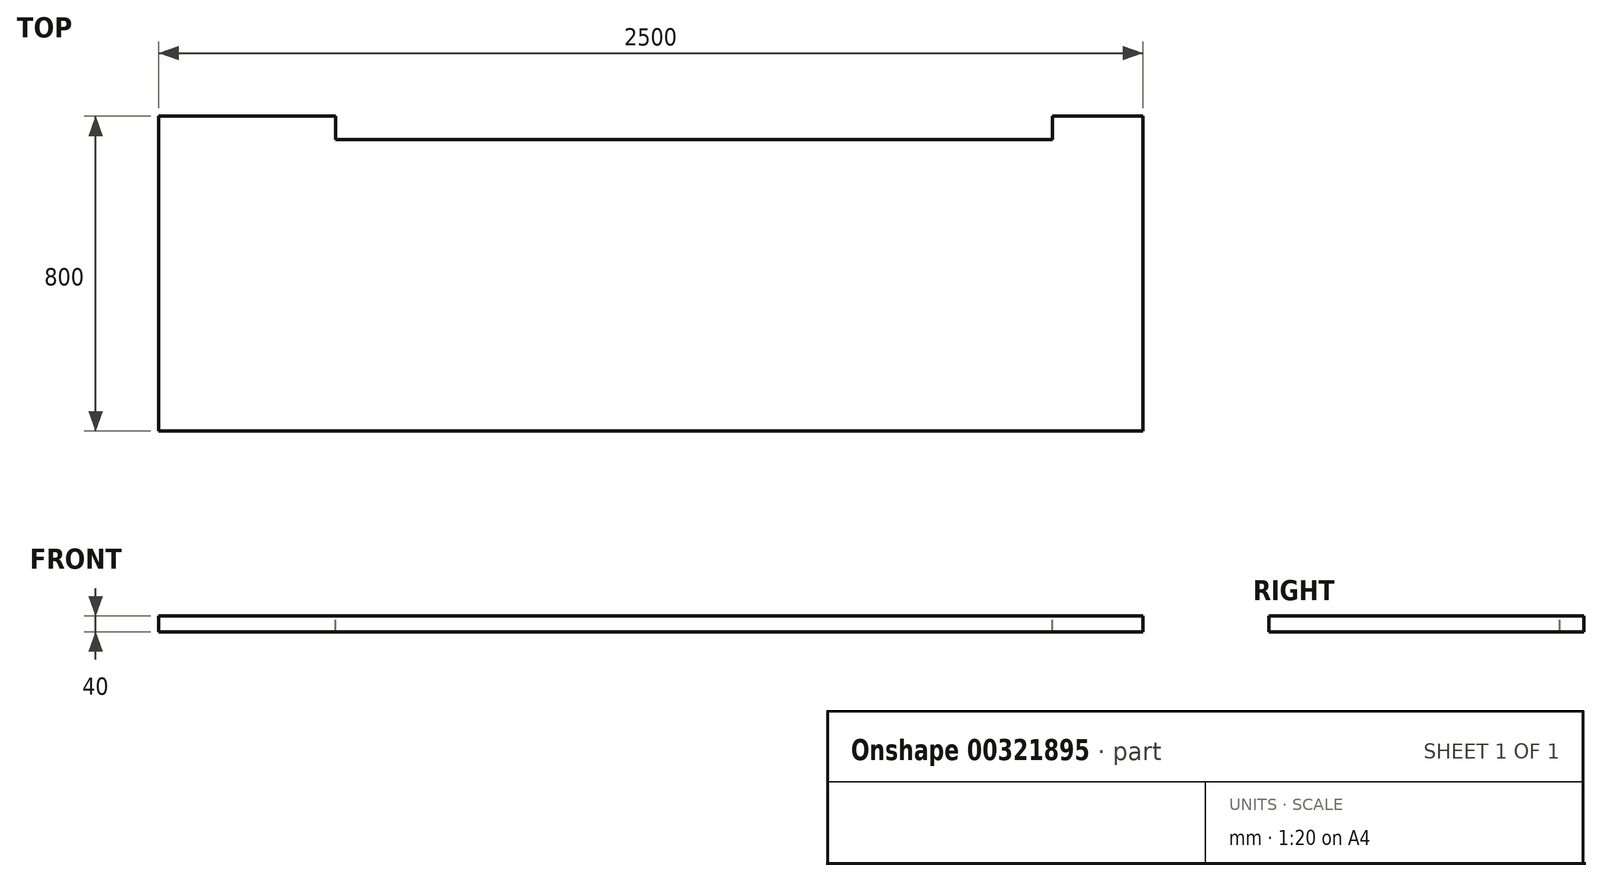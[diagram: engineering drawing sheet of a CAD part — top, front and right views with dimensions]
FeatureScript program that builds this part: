
annotation { "Feature Type Name" : "Feature", "Feature Type Description" : "" }
export const myFeature = defineFeature(function(context is Context, id is Id, definition is map)
    precondition{}
    {
        {
            var Q0;
            Q0=qCreatedBy(makeId("Top.planeOp"),FACE);
            var sketch = newSketch(context, id + "F0", { "sketchPlane" : qUnion([Q0])});
            skLineSegment(sketch, "E0.bottom", {"start": v(-2530.84, 807.52) * mm, "end": v(-30.84, 807.52) * mm});
            skLineSegment(sketch, "E0.top", {"start": v(-2530.84, 7.52) * mm, "end": v(-30.84, 7.52) * mm});
            skLineSegment(sketch, "E0.left", {"start": v(-2530.84, 807.52) * mm, "end": v(-2530.84, 7.52) * mm});
            skLineSegment(sketch, "E0.right", {"start": v(-30.84, 807.52) * mm, "end": v(-30.84, 7.52) * mm});
            skSolve(sketch);
        }
        {
            var Q0;
            Q0=makeQuery(id+"F0.imprint","IMPRINT",FACE,{"disambiguationData":[TD([[makeQuery(id+"F0.imprint","IMPRINT",EDGE,{"derivedFrom":sQuery(id+"F0.wireOp",EDGE,"E0.bottom")}),-1.0]])]});
            extrude(context, id + "F1", {"entities" : qUnion([Q0]), "depth" : 40 * mm});
        }
        {
            var Q0;
            Q0=makeQuery(id+"F1.opExtrude","CAP_FACE",FACE,{"disambiguationData":[OSD([sQuery(id+"F0.wireOp",EDGE,"E0.bottom"),sQuery(id+"F0.wireOp",EDGE,"E0.top"),sQuery(id+"F0.wireOp",EDGE,"E0.left"),sQuery(id+"F0.wireOp",EDGE,"E0.right")])],"isStart":false});
            var sketch = newSketch(context, id + "F2", { "sketchPlane" : qUnion([Q0])});
            skLineSegment(sketch, "E1", {"start": v(-30.84, 807.52) * mm, "end": v(-260.84, 807.52) * mm});
            skLineSegment(sketch, "E2.bottom", {"start": v(-260.84, 807.52) * mm, "end": v(-2080.84, 807.52) * mm});
            skLineSegment(sketch, "E2.top", {"start": v(-260.84, 747.52) * mm, "end": v(-2080.84, 747.52) * mm});
            skLineSegment(sketch, "E2.left", {"start": v(-260.84, 807.52) * mm, "end": v(-260.84, 747.52) * mm});
            skLineSegment(sketch, "E2.right", {"start": v(-2080.84, 807.52) * mm, "end": v(-2080.84, 747.52) * mm});
            skSolve(sketch);
        }
        {
            var Q0;
            Q0=makeQuery(id+"F2.imprint","IMPRINT",FACE,{"disambiguationData":[TD([[makeQuery(id+"F2.imprint","IMPRINT",EDGE,{"derivedFrom":sQuery(id+"F2.wireOp",EDGE,"E2.bottom")}),-1.0]])]});
            extrude(context, id + "F3", {"entities" : qUnion([Q0]), "operationType" : NewBodyOperationType.REMOVE, "oppositeDirection" : true, "depth" : 40 * mm});
        }
    });
